annotation { "Feature Type Name" : "Feature", "Feature Type Description" : "" }
export const myFeature = defineFeature(function(context is Context, id is Id, definition is map)
    precondition{}
    {
        {
            var Q0;
            Q0=qCreatedBy(makeId("Top.planeOp"),FACE);
            var sketch = newSketch(context, id + "F0", { "sketchPlane" : qUnion([Q0])});
            skLineSegment(sketch, "E0.bottom", {"start": v(-139.49, 44.04) * mm, "end": v(5.51, 44.04) * mm});
            skLineSegment(sketch, "E0.top", {"start": v(-109.49, -55.96) * mm, "end": v(5.51, -55.96) * mm});
            skLineSegment(sketch, "E0.left", {"start": v(-149.49, 34.04) * mm, "end": v(-149.49, -55.96) * mm});
            skLineSegment(sketch, "E0.right", {"start": v(15.51, 34.04) * mm, "end": v(15.51, -45.96) * mm});
            skText(sketch, "E1", { "text": "CHAOS WG", "fontName": "AllertaStencil-Regular.ttf"});
            skLineSegment(sketch, "E2.top", {"start": v(-139.49, -105.96) * mm, "end": v(-129.49, -105.96) * mm});
            skLineSegment(sketch, "E2.left", {"start": v(-149.49, -55.96) * mm, "end": v(-149.49, -95.96) * mm});
            skLineSegment(sketch, "E2.right", {"start": v(-119.49, -65.96) * mm, "end": v(-119.49, -95.96) * mm});
            skPoint(sketch, "E3.visualSharp", {"position": v(-149.49, -105.96) * mm});
            skArc(sketch, "E3.filletArc", {"start": v(-149.49, -95.96) * mm, "mid": v(-146.56, -103.03) * mm, "end": v(-139.49, -105.96) * mm});
            skPoint(sketch, "E4.visualSharp", {"position": v(-119.49, -105.96) * mm});
            skArc(sketch, "E4.filletArc", {"start": v(-129.49, -105.96) * mm, "mid": v(-122.42, -103.03) * mm, "end": v(-119.49, -95.96) * mm});
            skLineSegment(sketch, "E5", {"start": v(-119.49, -55.96) * mm, "end": v(-149.49, -55.96) * mm});
            skPoint(sketch, "E6.visualSharp", {"position": v(-149.49, 44.04) * mm});
            skArc(sketch, "E6.filletArc", {"start": v(-139.49, 44.04) * mm, "mid": v(-146.56, 41.11) * mm, "end": v(-149.49, 34.04) * mm});
            skPoint(sketch, "E7.visualSharp", {"position": v(15.51, 44.04) * mm});
            skArc(sketch, "E7.filletArc", {"start": v(15.51, 34.04) * mm, "mid": v(12.58, 41.11) * mm, "end": v(5.51, 44.04) * mm});
            skPoint(sketch, "E8.visualSharp", {"position": v(15.51, -55.96) * mm});
            skArc(sketch, "E8.filletArc", {"start": v(5.51, -55.96) * mm, "mid": v(12.58, -53.03) * mm, "end": v(15.51, -45.96) * mm});
            skPoint(sketch, "E9.visualSharp", {"position": v(-119.49, -55.96) * mm});
            skArc(sketch, "E9.filletArc", {"start": v(-109.49, -55.96) * mm, "mid": v(-116.56, -58.89) * mm, "end": v(-119.49, -65.96) * mm});
            skCircle(sketch, "E10", {"center": v(-134.49, -92.88) * mm, "radius": 5 * mm});
            skPoint(sketch, "E10.centerSnap0", {"position": v(-134.49, -105.96) * mm});
            skLineSegment(sketch, "E11", {"start": v(-17.63, 2) * mm, "end": v(-17.63, 44.04) * mm, "construction": true});
            skLineSegment(sketch, "E12", {"start": v(-17.63, -13.92) * mm, "end": v(-17.63, -55.96) * mm, "construction": true});
            skLineSegment(sketch, "E13", {"start": v(-149.49, -4.4) * mm, "end": v(-126.99, -4.4) * mm, "construction": true});
            skLineSegment(sketch, "E14", {"start": v(-6.99, -4.4) * mm, "end": v(15.51, -4.4) * mm, "construction": true});
            skPoint(sketch, "E14.startSnap0", {"position": v(-6.99, -5.96) * mm});
            const initialGuessF0  = {"E1": [-0.12699, -0.01392, 1, 0, 0.01593]};
            skSetInitialGuess(sketch, initialGuessF0);
            skSolve(sketch);
        }
        {
            var Q0;
            Q0=makeQuery(id+"F0.imprint","IMPRINT",FACE,{"disambiguationData":[TD([[makeQuery(id+"F0.imprint","IMPRINT",EDGE,{"derivedFrom":sQuery(id+"F0.wireOp",EDGE,"E0.bottom")}),-1.0]])]});
            var Q1;
            Q1=makeQuery(id+"F0.imprint","IMPRINT",FACE,{"disambiguationData":[TD([[makeQuery(id+"F0.imprint","IMPRINT",EDGE,{"derivedFrom":sQuery(id+"F0.wireOp",EDGE,"E2.top")}),1.0]])]});
            extrude(context, id + "F1", {"entities" : qUnion([Q0, Q1]), "depth" : 1.2 * mm, "offsetDistance" : 25 * mm});
        }
        {
            var Q0;
            Q0=makeQuery(id+"F1.opExtrude","CAP_FACE",FACE,{"disambiguationData":[OSD([sQuery(id+"F0.wireOp",EDGE,"E0.bottom"),sQuery(id+"F0.wireOp",EDGE,"E0.top"),sQuery(id+"F0.wireOp",EDGE,"E0.left"),sQuery(id+"F0.wireOp",EDGE,"E0.right"),sQuery(id+"F0.wireOp",EDGE,"E1.sketch_text.stroke-0"),sQuery(id+"F0.wireOp",EDGE,"E1.sketch_text.stroke-1"),sQuery(id+"F0.wireOp",EDGE,"E1.sketch_text.stroke-2"),sQuery(id+"F0.wireOp",EDGE,"E1.sketch_text.stroke-3"),sQuery(id+"F0.wireOp",EDGE,"E1.sketch_text.stroke-4"),sQuery(id+"F0.wireOp",EDGE,"E1.sketch_text.stroke-5"),sQuery(id+"F0.wireOp",EDGE,"E1.sketch_text.stroke-6"),sQuery(id+"F0.wireOp",EDGE,"E1.sketch_text.stroke-7"),sQuery(id+"F0.wireOp",EDGE,"E1.sketch_text.stroke-8"),sQuery(id+"F0.wireOp",EDGE,"E1.sketch_text.stroke-9"),sQuery(id+"F0.wireOp",EDGE,"E1.sketch_text.stroke-10"),sQuery(id+"F0.wireOp",EDGE,"E1.sketch_text.stroke-11"),sQuery(id+"F0.wireOp",EDGE,"E1.sketch_text.stroke-12"),sQuery(id+"F0.wireOp",EDGE,"E1.sketch_text.stroke-13"),sQuery(id+"F0.wireOp",EDGE,"E1.sketch_text.stroke-14"),sQuery(id+"F0.wireOp",EDGE,"E1.sketch_text.stroke-15"),sQuery(id+"F0.wireOp",EDGE,"E1.sketch_text.stroke-16"),sQuery(id+"F0.wireOp",EDGE,"E1.sketch_text.stroke-17"),sQuery(id+"F0.wireOp",EDGE,"E1.sketch_text.stroke-18"),sQuery(id+"F0.wireOp",EDGE,"E1.sketch_text.stroke-19"),sQuery(id+"F0.wireOp",EDGE,"E1.sketch_text.stroke-20"),sQuery(id+"F0.wireOp",EDGE,"E1.sketch_text.stroke-21"),sQuery(id+"F0.wireOp",EDGE,"E1.sketch_text.stroke-23"),sQuery(id+"F0.wireOp",EDGE,"E1.sketch_text.stroke-24"),sQuery(id+"F0.wireOp",EDGE,"E1.sketch_text.stroke-25"),sQuery(id+"F0.wireOp",EDGE,"E1.sketch_text.stroke-26"),sQuery(id+"F0.wireOp",EDGE,"E1.sketch_text.stroke-27"),sQuery(id+"F0.wireOp",EDGE,"E1.sketch_text.stroke-28"),sQuery(id+"F0.wireOp",EDGE,"E1.sketch_text.stroke-29"),sQuery(id+"F0.wireOp",EDGE,"E1.sketch_text.stroke-30"),sQuery(id+"F0.wireOp",EDGE,"E1.sketch_text.stroke-31"),sQuery(id+"F0.wireOp",EDGE,"E1.sketch_text.stroke-32"),sQuery(id+"F0.wireOp",EDGE,"E1.sketch_text.stroke-33"),sQuery(id+"F0.wireOp",EDGE,"E1.sketch_text.stroke-34"),sQuery(id+"F0.wireOp",EDGE,"E1.sketch_text.stroke-35"),sQuery(id+"F0.wireOp",EDGE,"E1.sketch_text.stroke-36"),sQuery(id+"F0.wireOp",EDGE,"E1.sketch_text.stroke-37"),sQuery(id+"F0.wireOp",EDGE,"E1.sketch_text.stroke-38"),sQuery(id+"F0.wireOp",EDGE,"E1.sketch_text.stroke-39"),sQuery(id+"F0.wireOp",EDGE,"E1.sketch_text.stroke-40"),sQuery(id+"F0.wireOp",EDGE,"E1.sketch_text.stroke-41"),sQuery(id+"F0.wireOp",EDGE,"E1.sketch_text.stroke-42"),sQuery(id+"F0.wireOp",EDGE,"E1.sketch_text.stroke-43"),sQuery(id+"F0.wireOp",EDGE,"E1.sketch_text.stroke-44"),sQuery(id+"F0.wireOp",EDGE,"E1.sketch_text.stroke-45"),sQuery(id+"F0.wireOp",EDGE,"E1.sketch_text.stroke-46"),sQuery(id+"F0.wireOp",EDGE,"E1.sketch_text.stroke-47"),sQuery(id+"F0.wireOp",EDGE,"E1.sketch_text.stroke-48"),sQuery(id+"F0.wireOp",EDGE,"E1.sketch_text.stroke-49"),sQuery(id+"F0.wireOp",EDGE,"E1.sketch_text.stroke-50"),sQuery(id+"F0.wireOp",EDGE,"E1.sketch_text.stroke-51"),sQuery(id+"F0.wireOp",EDGE,"E1.sketch_text.stroke-52"),sQuery(id+"F0.wireOp",EDGE,"E1.sketch_text.stroke-53"),sQuery(id+"F0.wireOp",EDGE,"E1.sketch_text.stroke-54"),sQuery(id+"F0.wireOp",EDGE,"E1.sketch_text.stroke-55"),sQuery(id+"F0.wireOp",EDGE,"E1.sketch_text.stroke-56"),sQuery(id+"F0.wireOp",EDGE,"E1.sketch_text.stroke-57"),sQuery(id+"F0.wireOp",EDGE,"E1.sketch_text.stroke-58"),sQuery(id+"F0.wireOp",EDGE,"E1.sketch_text.stroke-59"),sQuery(id+"F0.wireOp",EDGE,"E1.sketch_text.stroke-60"),sQuery(id+"F0.wireOp",EDGE,"E1.sketch_text.stroke-61"),sQuery(id+"F0.wireOp",EDGE,"E1.sketch_text.stroke-62"),sQuery(id+"F0.wireOp",EDGE,"E1.sketch_text.stroke-63"),sQuery(id+"F0.wireOp",EDGE,"E1.sketch_text.stroke-64"),sQuery(id+"F0.wireOp",EDGE,"E1.sketch_text.stroke-65"),sQuery(id+"F0.wireOp",EDGE,"E1.sketch_text.stroke-66"),sQuery(id+"F0.wireOp",EDGE,"E1.sketch_text.stroke-67"),sQuery(id+"F0.wireOp",EDGE,"E1.sketch_text.stroke-68"),sQuery(id+"F0.wireOp",EDGE,"E1.sketch_text.stroke-69"),sQuery(id+"F0.wireOp",EDGE,"E1.sketch_text.stroke-70"),sQuery(id+"F0.wireOp",EDGE,"E1.sketch_text.stroke-71"),sQuery(id+"F0.wireOp",EDGE,"E1.sketch_text.stroke-72"),sQuery(id+"F0.wireOp",EDGE,"E1.sketch_text.stroke-73"),sQuery(id+"F0.wireOp",EDGE,"E1.sketch_text.stroke-74"),sQuery(id+"F0.wireOp",EDGE,"E1.sketch_text.stroke-75"),sQuery(id+"F0.wireOp",EDGE,"E1.sketch_text.stroke-76"),sQuery(id+"F0.wireOp",EDGE,"E1.sketch_text.stroke-77"),sQuery(id+"F0.wireOp",EDGE,"E1.sketch_text.stroke-78"),sQuery(id+"F0.wireOp",EDGE,"E1.sketch_text.stroke-79"),sQuery(id+"F0.wireOp",EDGE,"E1.sketch_text.stroke-80"),sQuery(id+"F0.wireOp",EDGE,"E1.sketch_text.stroke-81"),sQuery(id+"F0.wireOp",EDGE,"E1.sketch_text.stroke-82"),sQuery(id+"F0.wireOp",EDGE,"E1.sketch_text.stroke-83"),sQuery(id+"F0.wireOp",EDGE,"E1.sketch_text.stroke-84"),sQuery(id+"F0.wireOp",EDGE,"E1.sketch_text.stroke-85"),sQuery(id+"F0.wireOp",EDGE,"E1.sketch_text.stroke-86"),sQuery(id+"F0.wireOp",EDGE,"E1.sketch_text.stroke-87"),sQuery(id+"F0.wireOp",EDGE,"E1.sketch_text.stroke-88"),sQuery(id+"F0.wireOp",EDGE,"E1.sketch_text.stroke-89"),sQuery(id+"F0.wireOp",EDGE,"E1.sketch_text.stroke-90"),sQuery(id+"F0.wireOp",EDGE,"E1.sketch_text.stroke-91"),sQuery(id+"F0.wireOp",EDGE,"E1.sketch_text.stroke-92"),sQuery(id+"F0.wireOp",EDGE,"E1.sketch_text.stroke-93"),sQuery(id+"F0.wireOp",EDGE,"E1.sketch_text.stroke-94"),sQuery(id+"F0.wireOp",EDGE,"E1.sketch_text.stroke-95"),sQuery(id+"F0.wireOp",EDGE,"E1.sketch_text.stroke-96"),sQuery(id+"F0.wireOp",EDGE,"E1.sketch_text.stroke-97"),sQuery(id+"F0.wireOp",EDGE,"E1.sketch_text.stroke-98"),sQuery(id+"F0.wireOp",EDGE,"E1.sketch_text.stroke-99"),sQuery(id+"F0.wireOp",EDGE,"E1.sketch_text.stroke-100"),sQuery(id+"F0.wireOp",EDGE,"E1.sketch_text.stroke-101"),sQuery(id+"F0.wireOp",EDGE,"E1.sketch_text.stroke-102"),sQuery(id+"F0.wireOp",EDGE,"E1.sketch_text.stroke-103"),sQuery(id+"F0.wireOp",EDGE,"E1.sketch_text.stroke-104"),sQuery(id+"F0.wireOp",EDGE,"E1.sketch_text.stroke-105"),sQuery(id+"F0.wireOp",EDGE,"E1.sketch_text.stroke-106"),sQuery(id+"F0.wireOp",EDGE,"E1.sketch_text.stroke-107"),sQuery(id+"F0.wireOp",EDGE,"E1.sketch_text.stroke-108"),sQuery(id+"F0.wireOp",EDGE,"E1.sketch_text.stroke-109"),sQuery(id+"F0.wireOp",EDGE,"E1.sketch_text.stroke-110"),sQuery(id+"F0.wireOp",EDGE,"E1.sketch_text.stroke-111"),sQuery(id+"F0.wireOp",EDGE,"E1.sketch_text.stroke-112"),sQuery(id+"F0.wireOp",EDGE,"E1.sketch_text.stroke-113"),sQuery(id+"F0.wireOp",EDGE,"E1.sketch_text.stroke-114"),sQuery(id+"F0.wireOp",EDGE,"E1.sketch_text.stroke-115"),sQuery(id+"F0.wireOp",EDGE,"E1.sketch_text.stroke-116"),sQuery(id+"F0.wireOp",EDGE,"E1.sketch_text.stroke-117"),sQuery(id+"F0.wireOp",EDGE,"E1.sketch_text.stroke-118"),sQuery(id+"F0.wireOp",EDGE,"E1.sketch_text.stroke-119"),sQuery(id+"F0.wireOp",EDGE,"E1.sketch_text.stroke-120"),sQuery(id+"F0.wireOp",EDGE,"E1.sketch_text.stroke-121"),sQuery(id+"F0.wireOp",EDGE,"E1.sketch_text.stroke-122"),sQuery(id+"F0.wireOp",EDGE,"E1.sketch_text.stroke-123"),sQuery(id+"F0.wireOp",EDGE,"E1.sketch_text.stroke-124"),sQuery(id+"F0.wireOp",EDGE,"E1.sketch_text.stroke-125"),sQuery(id+"F0.wireOp",EDGE,"E1.sketch_text.stroke-126"),sQuery(id+"F0.wireOp",EDGE,"E1.sketch_text.stroke-127"),sQuery(id+"F0.wireOp",EDGE,"E1.sketch_text.stroke-128"),sQuery(id+"F0.wireOp",EDGE,"E1.sketch_text.stroke-129"),sQuery(id+"F0.wireOp",EDGE,"E1.sketch_text.stroke-130"),sQuery(id+"F0.wireOp",EDGE,"E1.sketch_text.stroke-131"),sQuery(id+"F0.wireOp",EDGE,"E1.sketch_text.stroke-132"),sQuery(id+"F0.wireOp",EDGE,"E1.sketch_text.stroke-133"),sQuery(id+"F0.wireOp",EDGE,"E1.sketch_text.stroke-134"),sQuery(id+"F0.wireOp",EDGE,"E1.sketch_text.stroke-135"),sQuery(id+"F0.wireOp",EDGE,"E1.sketch_text.stroke-136"),sQuery(id+"F0.wireOp",EDGE,"E1.sketch_text.stroke-137"),sQuery(id+"F0.wireOp",EDGE,"E1.sketch_text.stroke-138"),sQuery(id+"F0.wireOp",EDGE,"E1.sketch_text.stroke-139"),sQuery(id+"F0.wireOp",EDGE,"E1.sketch_text.stroke-140"),sQuery(id+"F0.wireOp",EDGE,"E1.sketch_text.stroke-141"),sQuery(id+"F0.wireOp",EDGE,"E1.sketch_text.stroke-142"),sQuery(id+"F0.wireOp",EDGE,"E1.sketch_text.stroke-143"),sQuery(id+"F0.wireOp",EDGE,"E1.sketch_text.stroke-144"),sQuery(id+"F0.wireOp",EDGE,"E1.sketch_text.stroke-145"),sQuery(id+"F0.wireOp",EDGE,"E1.sketch_text.stroke-146"),sQuery(id+"F0.wireOp",EDGE,"E1.sketch_text.stroke-147"),sQuery(id+"F0.wireOp",EDGE,"E1.sketch_text.stroke-148"),sQuery(id+"F0.wireOp",EDGE,"E1.sketch_text.stroke-149"),sQuery(id+"F0.wireOp",EDGE,"E1.sketch_text.stroke-150"),sQuery(id+"F0.wireOp",EDGE,"E1.sketch_text.stroke-151"),sQuery(id+"F0.wireOp",EDGE,"E1.sketch_text.stroke-152"),sQuery(id+"F0.wireOp",EDGE,"E1.sketch_text.stroke-153"),sQuery(id+"F0.wireOp",EDGE,"E1.sketch_text.stroke-154"),sQuery(id+"F0.wireOp",EDGE,"E1.sketch_text.stroke-155"),sQuery(id+"F0.wireOp",EDGE,"E1.sketch_text.stroke-156"),sQuery(id+"F0.wireOp",EDGE,"E1.sketch_text.stroke-157"),sQuery(id+"F0.wireOp",EDGE,"E1.sketch_text.stroke-158"),sQuery(id+"F0.wireOp",EDGE,"E1.sketch_text.stroke-159"),sQuery(id+"F0.wireOp",EDGE,"E1.sketch_text.stroke-160"),sQuery(id+"F0.wireOp",EDGE,"E1.sketch_text.stroke-161"),sQuery(id+"F0.wireOp",EDGE,"E1.sketch_text.stroke-162"),sQuery(id+"F0.wireOp",EDGE,"E1.sketch_text.stroke-163"),sQuery(id+"F0.wireOp",EDGE,"E1.sketch_text.stroke-164"),sQuery(id+"F0.wireOp",EDGE,"E1.sketch_text.stroke-165"),sQuery(id+"F0.wireOp",EDGE,"E1.sketch_text.stroke-166"),sQuery(id+"F0.wireOp",EDGE,"E1.sketch_text.stroke-167"),sQuery(id+"F0.wireOp",EDGE,"E2.top"),sQuery(id+"F0.wireOp",EDGE,"E2.left"),sQuery(id+"F0.wireOp",EDGE,"E2.right"),sQuery(id+"F0.wireOp",EDGE,"E3.filletArc"),sQuery(id+"F0.wireOp",EDGE,"E4.filletArc"),sQuery(id+"F0.wireOp",EDGE,"E6.filletArc"),sQuery(id+"F0.wireOp",EDGE,"E7.filletArc"),sQuery(id+"F0.wireOp",EDGE,"E8.filletArc"),sQuery(id+"F0.wireOp",EDGE,"E9.filletArc"),sQuery(id+"F0.wireOp",EDGE,"E10"),sQuery(id+"F0.wireOp",EDGE,"qL5VfvvJ-fDNp-9u9I-rb3k-eRDdlZV9wKvX")])],"isStart":false});
            shell(context, id + "F2", {"entities" : qUnion([Q0]), "thickness" : 0.9 * mm});
        }
    });